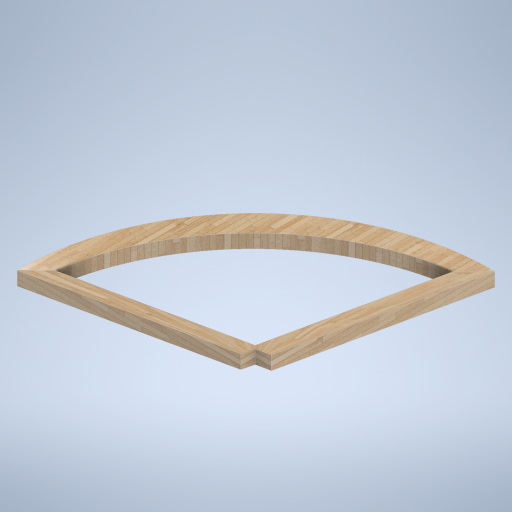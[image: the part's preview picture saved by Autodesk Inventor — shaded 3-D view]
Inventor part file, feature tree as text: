
AUTODESK INVENTOR PART (.ipt)
format: ipt  version: 2024.2 (Build 282272000, 272)  size: 412,672 bytes
history: native  units: mm
features: sketch x12, plane x6, extrude x3, projected_geometry x3, loft x2
ambient origin geometry x8: Origin, YZ Plane, XZ Plane, XY Plane, X Axis, Y Axis, Z Axis, Center Point
bodies: Solid1 (feature_tree)
feature tree (26):
  sketch  "Sketch1"  dims[d0=2449.0mm d1=2449.0mm]
  plane  "Work Plane1"
  plane  "Work Plane2"
  sketch  "Sketch2"  dims[d2=2600.0mm d3=0.0mm d4=177.610858mm]
  plane  "Work Plane3"
  sketch  "Sketch4"  dims[d5=157.312474mm d6=90.0deg]
  plane  "Work Plane4"
  sketch  "Sketch5"  dims[d7=150.0mm d8=29.670597mm]
  extrude  "Extrusion1"  Depth=2449.0mm
  plane  "Work Plane5"
  sketch  "Sketch6"  dims[d9=29.670597mm d10=90.0deg]
  sketch  "Sketch7"  dims[d11=150.0mm]
  sketch  "Sketch8"  dims[d12=1.745329mm]
  plane  "Work Plane6"
  sketch  "Sketch9"  dims[d13=1.745329mm]
  loft  "Loft1"
  loft  "Loft2"
  extrude  "Extrusion2"  Depth=29.670597mm
  extrude  "Extrusion3"  TaperAngle=90.0deg  [1 undecoded]
  projected_geometry  "Projected Loop1"
  projected_geometry  "Projected Loop2"
  sketch  "Sketch10"  dims[d14=-1000.0mm]
  sketch  "Sketch11"  dims[d15=582.0mm d16=0.0mm]
  sketch  "Sketch12"  dims[d17=0.0mm]
  projected_geometry  "Projected Loop3"
  sketch  "Sketch14"  dims[d18=29.670597mm d19=1.745329mm d20=-432.0mm d21=0.0mm d22=90.0deg d23=0.0mm d24=90.0deg d25=29.670597mm d26=1.745329mm d27=0.0mm d28=90.0deg d29=0.0mm d30=90.0deg d31=432.0mm d32=0.0mm d33=50.0mm d34=50.0mm d35=2600.0mm d36=432.0mm d37=0.0mm d38=500.0mm d39=0.872665mm]
note: 1 required parameter value undecoded (feature->parameter linkage not recoverable at this tier; creation-order binding heuristic only, values carry confidence <= 0.55)
